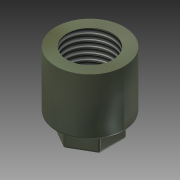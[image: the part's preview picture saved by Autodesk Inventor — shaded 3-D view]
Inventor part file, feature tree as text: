
AUTODESK INVENTOR PART (.ipt)
format: ipt  version: 2015 (Build 190159000, 159)  size: 139,776 bytes
history: native  units: mm
features: extrude x3, sketch x3, thread x1, fillet x1
ambient origin geometry x8: Origin, YZ Plane, XZ Plane, XY Plane, X Axis, Y Axis, Z Axis, Center Point
bodies: 实体1 (feature_tree)
feature tree (8):
  extrude  "拉伸1"  Depth=25.0mm TaperAngle=0.0deg
  extrude  "拉伸2"  Depth=20.0mm TaperAngle=0.0deg
  thread  "螺纹1"  [1 undecoded]
  extrude  "拉伸3"  Depth=8.0mm TaperAngle=0.0deg
  fillet  "圆角1"  Radius=1.0mm
  sketch  "草图1"  dims[d0=30.0mm d1=25.0mm d2=0.0mm]
  sketch  "草图2"  dims[d3=20.0mm d4=20.0mm d5=0.0mm d6=10.0mm d7=0.0mm]
  sketch  "草图3"  dims[d8=20.0mm d9=8.0mm d10=0.0mm d11=1.0mm]
note: 1 required parameter value undecoded (feature->parameter linkage not recoverable at this tier; creation-order binding heuristic only, values carry confidence <= 0.55)
